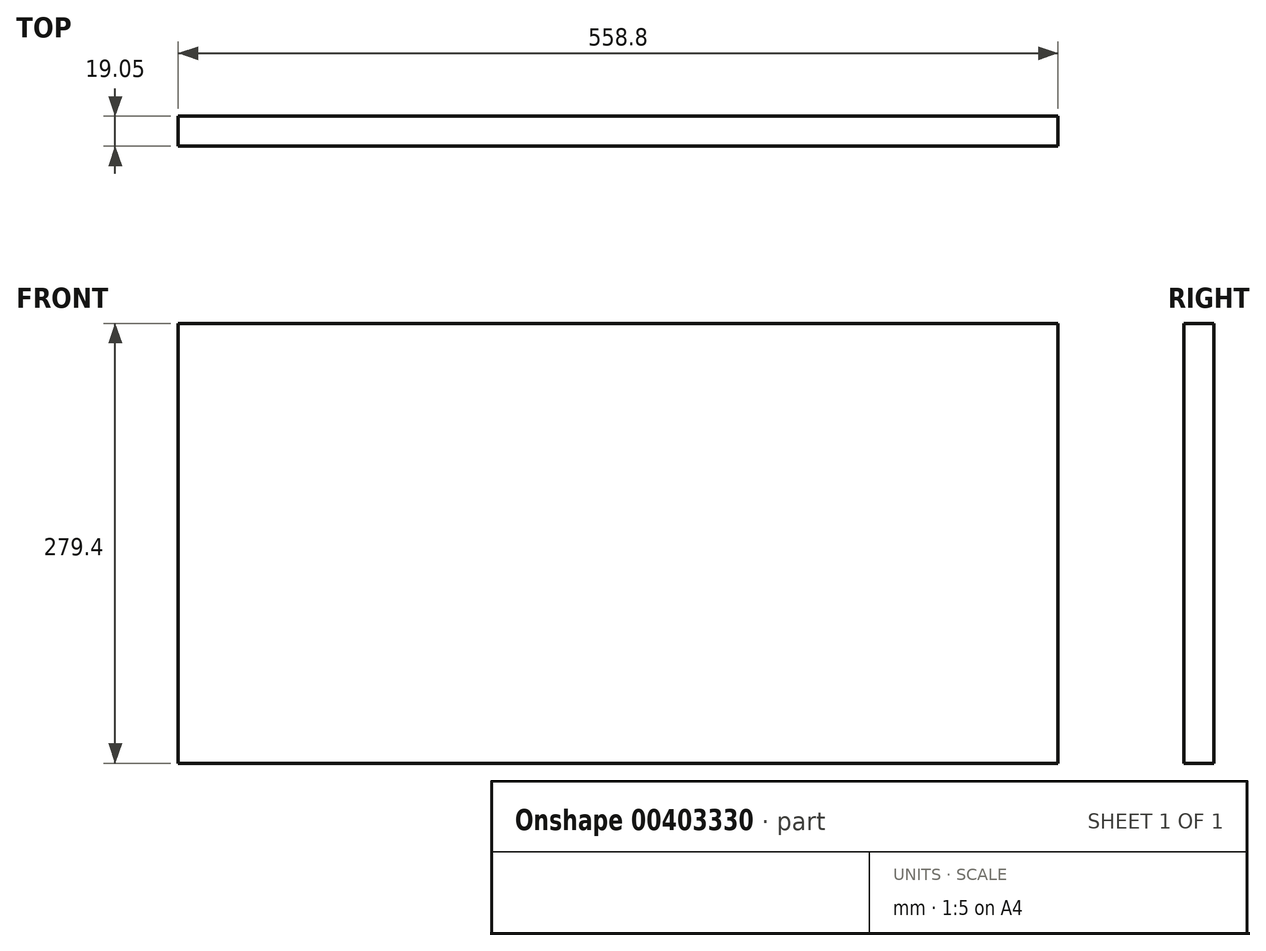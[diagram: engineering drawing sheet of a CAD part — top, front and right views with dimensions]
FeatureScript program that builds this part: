
annotation { "Feature Type Name" : "Feature", "Feature Type Description" : "" }
export const myFeature = defineFeature(function(context is Context, id is Id, definition is map)
    precondition{}
    {
        {
            var Q0;
            Q0=qCreatedBy(makeId("Front.planeOp"),FACE);
            var sketch = newSketch(context, id + "F0", { "sketchPlane" : qUnion([Q0])});
            skLineSegment(sketch, "E0.bottom", {"start": v(0, 0) * mm, "end": v(-558.8, 0) * mm});
            skLineSegment(sketch, "E0.top", {"start": v(0, 279.4) * mm, "end": v(-558.8, 279.4) * mm});
            skLineSegment(sketch, "E0.left", {"start": v(0, 0) * mm, "end": v(0, 279.4) * mm});
            skLineSegment(sketch, "E0.right", {"start": v(-558.8, 0) * mm, "end": v(-558.8, 279.4) * mm});
            skSolve(sketch);
        }
        {
            var Q0;
            Q0 = qSketchRegion(id + "F0", true);
            extrude(context, id + "F1", {"entities" : qUnion([Q0]), "depth" : 19.05 * mm});
        }
    });
